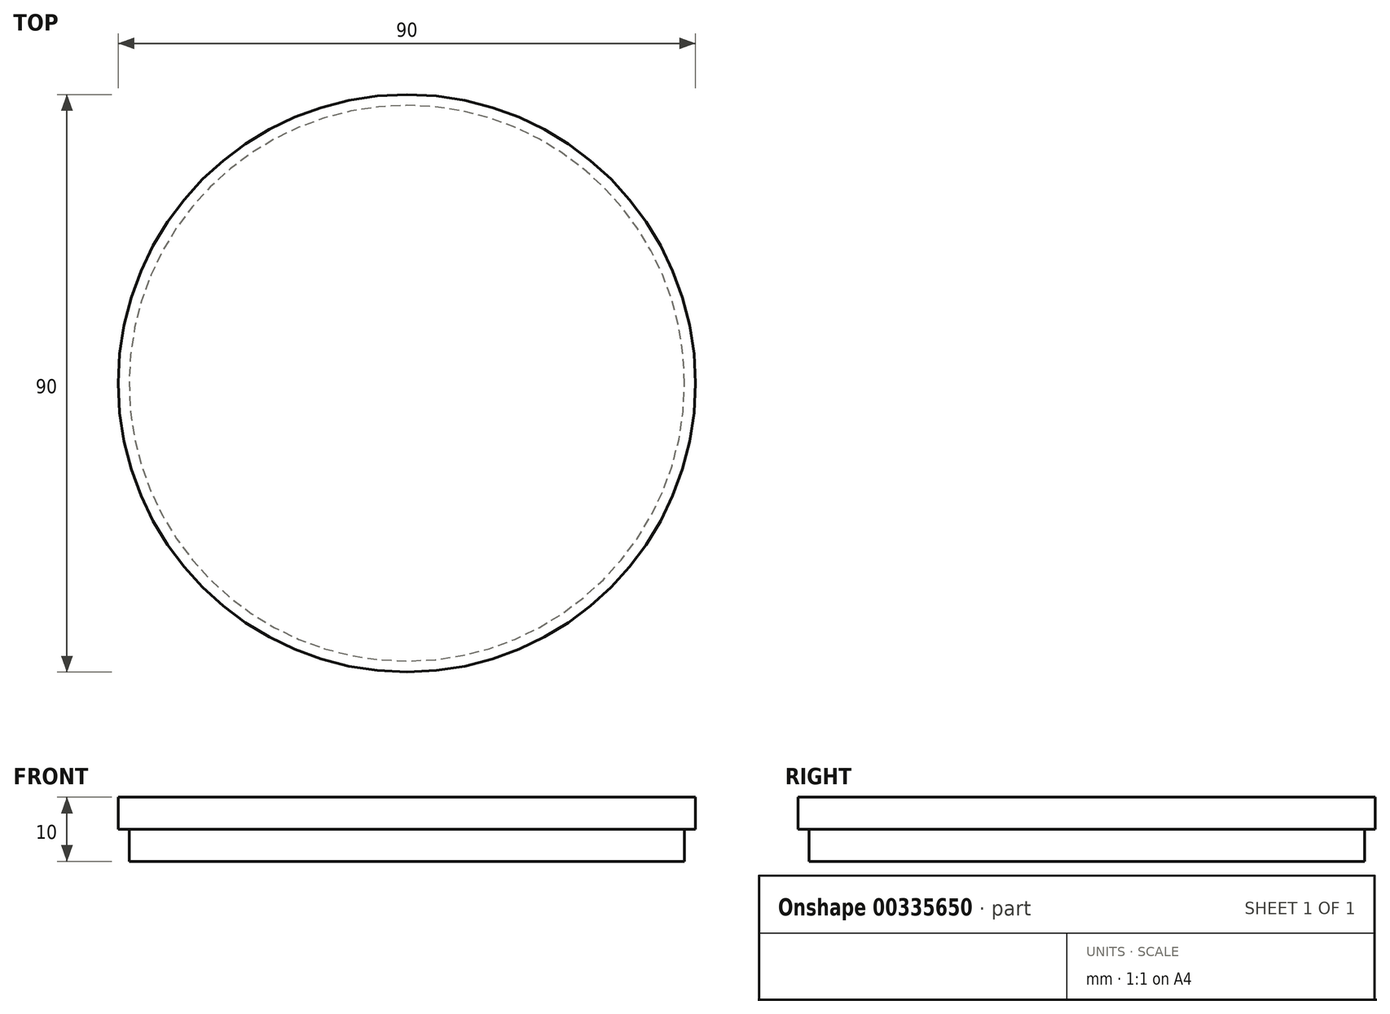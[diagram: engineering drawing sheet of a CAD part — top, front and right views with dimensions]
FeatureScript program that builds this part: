
annotation { "Feature Type Name" : "Feature", "Feature Type Description" : "" }
export const myFeature = defineFeature(function(context is Context, id is Id, definition is map)
    precondition{}
    {
        {
            var Q0;
            Q0=qCreatedBy(makeId("Top.planeOp"),FACE);
            var sketch = newSketch(context, id + "F0", { "sketchPlane" : qUnion([Q0])});
            skCircle(sketch, "E0", {"center": v(0, 0) * mm, "radius": 45 * mm});
            skSolve(sketch);
        }
        {
            var Q0;
            Q0 = qSketchRegion(id + "F0", true);
            extrude(context, id + "F1", {"entities" : qUnion([Q0]), "depth" : 5 * mm});
        }
        {
            var Q0;
            Q0=makeQuery(id+"F1.opExtrude","CAP_FACE",FACE,{"disambiguationData":[OSD([sQuery(id+"F0.wireOp",EDGE,"E0")])],"isStart":true});
            var sketch = newSketch(context, id + "F2", { "sketchPlane" : qUnion([Q0])});
            skCircle(sketch, "E1", {"center": v(0, 0) * mm, "radius": 43.3 * mm});
            skSolve(sketch);
        }
        {
            var Q0;
            Q0=makeQuery(id+"F2.imprint","IMPRINT",FACE,{"disambiguationData":[TD([[makeQuery(id+"F2.imprint","IMPRINT",EDGE,{"derivedFrom":sQuery(id+"F2.wireOp",EDGE,"E1")}),1.0]])]});
            extrude(context, id + "F3", {"entities" : qUnion([Q0]), "operationType" : NewBodyOperationType.ADD, "depth" : 5 * mm});
        }
    });
